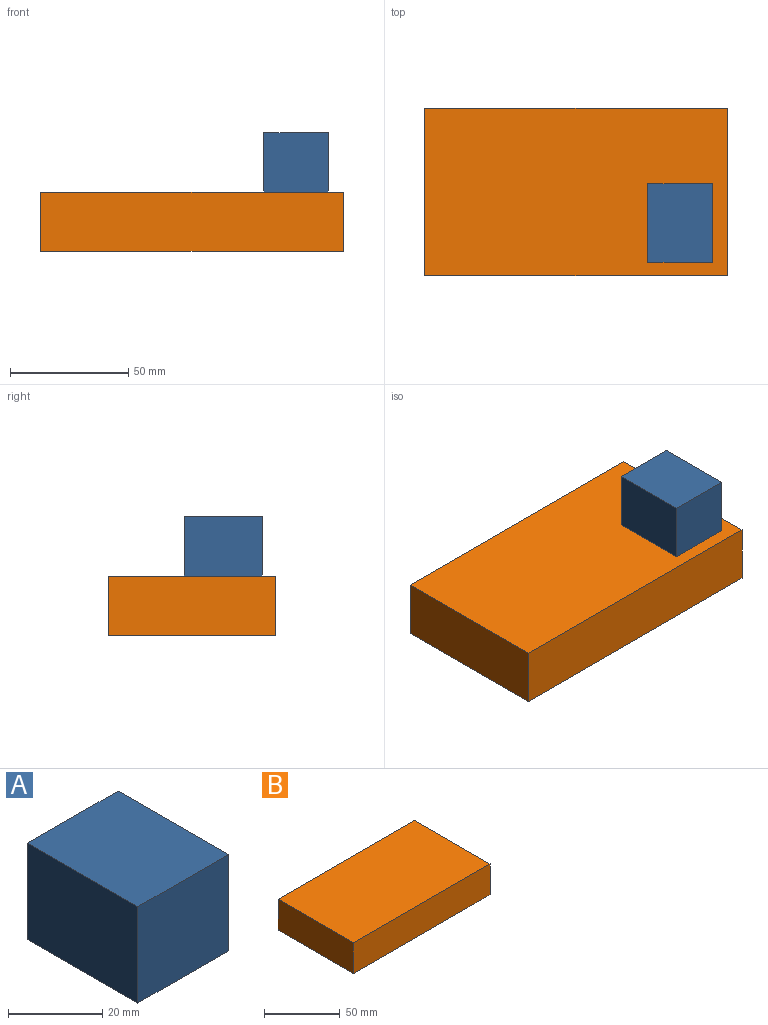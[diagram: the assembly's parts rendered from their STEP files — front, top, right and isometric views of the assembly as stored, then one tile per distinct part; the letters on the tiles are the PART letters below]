
ASSEMBLY  parts=2 mates=1
PART A: 6 faces, bbox 27.1x33x25 mm
  f0: plane 27.05x25mm, normal (0,-1,0), area 676.3mm2, adj f1,f3,f4,f5
  f1: plane 33.01x25mm, normal (1,0,0), area 825.4mm2, adj f0,f2,f4,f5
  f2: plane 27.05x25mm, normal (0,1,0), area 676.3mm2, adj f1,f3,f4,f5
  f3: plane 33.01x25mm, normal (-1,0,0), area 825.4mm2, adj f0,f2,f4,f5
  f4: plane 33.01x27.05mm, normal (0,0,1), area 893mm2, adj f0,f1,f2,f3
  f5: plane 33.01x27.05mm, normal (0,0,-1), area 893mm2, adj f0,f1,f2,f3
PART B: 6 faces, bbox 127.7x70.6x25 mm
  f0: plane 127.74x25mm, normal (0,1,0), area 3193.4mm2, adj f1,f3,f4,f5
  f1: plane 70.63x25mm, normal (-1,0,0), area 1765.7mm2, adj f0,f2,f4,f5
  f2: plane 127.74x25mm, normal (0,-1,0), area 3193.4mm2, adj f1,f3,f4,f5
  f3: plane 70.63x25mm, normal (1,0,0), area 1765.7mm2, adj f0,f2,f4,f5
  f4: plane 127.74x70.63mm, normal (0,0,1), area 9021.8mm2, adj f0,f1,f2,f3
  f5: plane 127.74x70.63mm, normal (0,0,-1), area 9021.8mm2, adj f0,f1,f2,f3
PLACE A t=(107.81,22.14,37.5)mm
PLACE B t=(63.87,35.31,12.5)mm
MATE planar B.f4 <-> A.f5  axis (0,0,1) through (63.87,35.31,25)mm
